# Revit family: SNS Mini Merlin CO2 AVG TFT Monitor
name_source: partatom
category: Electrical Equipment
units: mm (PartAtom-declared; Revit-internal decimal feet)

## family parameters
Always vertical = Yes
Cut with Voids When Loaded = No
OmniClass Number = 23.80.30.11.17
OmniClass Title = Distribution Boards and Control Panels
Part Type = Other Panel
Room Calculation Point = No
Round Connector Dimension = Use Diameter
Shared = No
Work Plane-Based = No

## types (1)
- SNS Merlin CO2 24hr AVG TFT Monitor
    Default Height = 4' - 0"
    Description = The Merlin CO2 AVG Monitor has a TFT display to show the user a clear and precise reading of the CO2 level in the room and average CO2 level over 24 & 8 hours. The monitor also provides statistics for the highest reading over a 24 hour period along with a colour system indicating the air quality in the area.
    Load = 120 VA
    Manufacturer = S&S Northern Ltd.
    Model = SNS Merlin CO2 24hr AVG TFT Monitor
    Product Information = https://snsnorthern.com
    Type Comments = The Merlin CO2 AVG Monitor has a TFT display to show the user a clear and precise reading of the CO2 level in the room and average CO2 level over 24 & 8 hours. The monitor also provides statistics for the highest reading over a 24 hour period along with a colour system indicating the air quality in the area.
    URL = https://snsnorthern.com
    Voltage = 120VAC

## geometry (parser evidence)
native form markers: Sweep x15
no freeform markers — native parametric forms only
